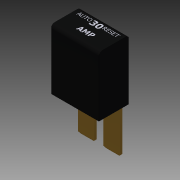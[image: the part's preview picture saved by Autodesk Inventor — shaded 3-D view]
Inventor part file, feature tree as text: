
AUTODESK INVENTOR PART (.ipt)
format: ipt  version: 2018 (Build 220112000, 112)  size: 481,792 bytes
history: native  units: in
note: dims shown in document units (in); Inventor stores cm internally (conversion verified against a paired STEP export)
features: sketch x6, extrude x4, plane x3, emboss x2, fillet x1, mirror x1
ambient origin geometry x8: Origin, YZ Plane, XZ Plane, XY Plane, X Axis, Y Axis, Z Axis, Center Point
bodies: Solid1 (feature_tree)
feature tree (17):
  extrude  "Extrusion1"  Depth=0.39in
  fillet  "Fillet1"  Radius=0.78in
  extrude  "Extrusion3"  Depth=0.212in
  extrude  "Extrusion4"  Depth=0.0585in
  extrude  "Extrusion5"  Depth=0.57in TaperAngle=0.0deg
  plane  "Work Plane1"
  mirror  "Mirror1"
  plane  "Work Plane2"
  emboss  "Emboss1"
  plane  "Work Plane4"
  emboss  "Emboss3"
  sketch  "Sketch1"  dims[d0=0.62in d1=0.39in d2=0.78in d3=0.0in]
  sketch  "Sketch2"  dims[d4=0.01in d5=0.05in d6=0.212in]
  sketch  "Sketch3"  dims[d8=0.031in d13=0.0585in]
  sketch  "Sketch4"  dims[d14=0.57in d15=0.0in d16=0.57in d17=0.0in]
  sketch  "Sketch6"  dims[d18=0.023in]
  sketch  "Sketch8"  dims[d19=0.023in d20=0.023in d21=0.57in d22=0.0in d26=0.1875in d27=0.0001in d28=0.0in d32=0.1875in d33=0.0001in d34=0.0in]
